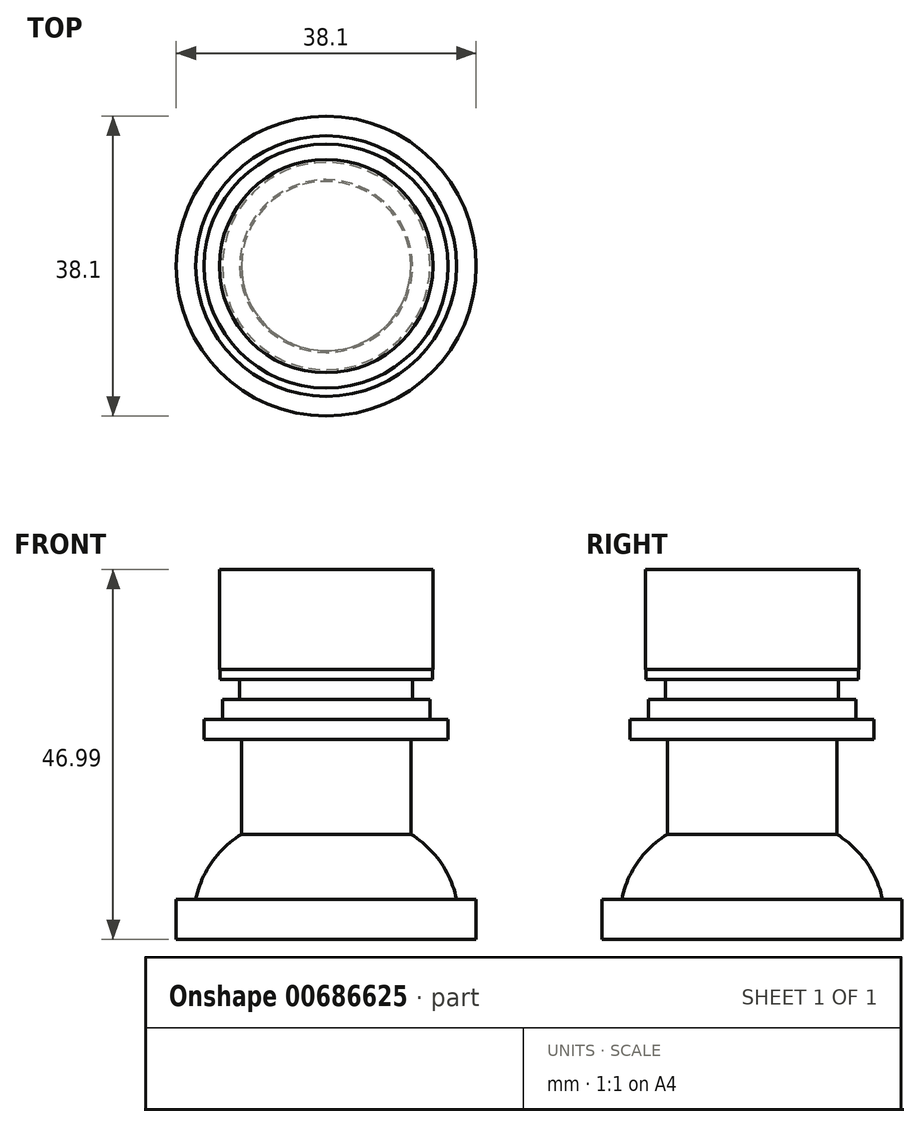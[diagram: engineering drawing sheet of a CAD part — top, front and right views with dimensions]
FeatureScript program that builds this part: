
annotation { "Feature Type Name" : "Feature", "Feature Type Description" : "" }
export const myFeature = defineFeature(function(context is Context, id is Id, definition is map)
    precondition{}
    {
        {
            var Q0;
            Q0=qCreatedBy(makeId("Top.planeOp"),FACE);
            var sketch = newSketch(context, id + "F0", { "sketchPlane" : qUnion([Q0])});
            skCircle(sketch, "E0", {"center": v(0, 0) * mm, "radius": 19.05 * mm});
            skSolve(sketch);
        }
        {
            var Q0;
            Q0=qCreatedBy(makeId("Top.planeOp"),FACE);
            var sketch = newSketch(context, id + "F1", { "sketchPlane" : qUnion([Q0])});
            skCircle(sketch, "E1", {"center": v(0, 0) * mm, "radius": 16.56 * mm});
            skSolve(sketch);
        }
        {
            var Q0;
            Q0 = qSketchRegion(id + "F0", true);
            extrude(context, id + "F2", {"entities" : qUnion([Q0]), "depth" : 5.08 * mm, "offsetDistance" : 25.4 * mm});
        }
        {
            var Q0;
            Q0 = qSketchRegion(id + "F1", true);
            extrude(context, id + "F3", {"entities" : qUnion([Q0]), "operationType" : NewBodyOperationType.ADD, "depth" : 15.24 * mm, "offsetDistance" : 25.4 * mm});
        }
        {
            var Q0;
            Q0=makeQuery(id+"F3.opExtrude","CAP_EDGE",EDGE,{"disambiguationData":[OSD([sQuery(id+"F1.wireOp",EDGE,"E1")])],"isStart":false});
            fillet(context, id + "F4", {"entities" : qUnion([Q0]), "radius" : 12.7 * mm, "tangentPropagation" : true, "allowEdgeOverflow" : false});
        }
        {
            var Q0;
            Q0=qCreatedBy(makeId("Top.planeOp"),FACE);
            var sketch = newSketch(context, id + "F5", { "sketchPlane" : qUnion([Q0])});
            skCircle(sketch, "E2", {"center": v(0, 0) * mm, "radius": 10.76 * mm});
            skSolve(sketch);
        }
        {
            var Q0;
            Q0 = qSketchRegion(id + "F5", true);
            extrude(context, id + "F6", {"entities" : qUnion([Q0]), "operationType" : NewBodyOperationType.ADD, "depth" : 25.4 * mm, "offsetDistance" : 25.4 * mm});
        }
        {
            var Q0;
            Q0=makeQuery(id+"F6.opExtrude","CAP_FACE",FACE,{"disambiguationData":[OSD([sQuery(id+"F5.wireOp",EDGE,"E2")])],"isStart":false});
            var sketch = newSketch(context, id + "F7", { "sketchPlane" : qUnion([Q0])});
            skCircle(sketch, "E3", {"center": v(0, 0) * mm, "radius": 15.5 * mm});
            skSolve(sketch);
        }
        {
            var Q0;
            Q0 = qSketchRegion(id + "F7", true);
            extrude(context, id + "F8", {"entities" : qUnion([Q0]), "operationType" : NewBodyOperationType.ADD, "depth" : 2.54 * mm, "offsetDistance" : 25.4 * mm});
        }
        {
            var Q0;
            Q0=makeQuery(id+"F8.opExtrude","CAP_FACE",FACE,{"disambiguationData":[OSD([sQuery(id+"F7.wireOp",EDGE,"E3")])],"isStart":false});
            var sketch = newSketch(context, id + "F9", { "sketchPlane" : qUnion([Q0])});
            skCircle(sketch, "E4", {"center": v(0, 0) * mm, "radius": 13.17 * mm});
            skSolve(sketch);
        }
        {
            var Q0;
            Q0 = qSketchRegion(id + "F9", true);
            extrude(context, id + "F10", {"entities" : qUnion([Q0]), "operationType" : NewBodyOperationType.ADD, "depth" : 2.54 * mm, "offsetDistance" : 25.4 * mm});
        }
        {
            var Q0;
            Q0=makeQuery(id+"F10.opExtrude","CAP_FACE",FACE,{"disambiguationData":[OSD([sQuery(id+"F9.wireOp",EDGE,"E4")])],"isStart":false});
            var sketch = newSketch(context, id + "F11", { "sketchPlane" : qUnion([Q0])});
            skCircle(sketch, "E5", {"center": v(0, 0) * mm, "radius": 10.98 * mm});
            skSolve(sketch);
        }
        {
            var Q0;
            Q0=makeQuery(id+"F11.imprint","IMPRINT",FACE,{"disambiguationData":[TD([[makeQuery(id+"F11.imprint","IMPRINT",EDGE,{"derivedFrom":sQuery(id+"F11.wireOp",EDGE,"E5")}),1.0]])]});
            extrude(context, id + "F12", {"entities" : qUnion([Q0]), "operationType" : NewBodyOperationType.ADD, "depth" : 2.54 * mm, "offsetDistance" : 25.4 * mm});
        }
        {
            var Q0;
            Q0=makeQuery(id+"F12.opExtrude","CAP_FACE",FACE,{"disambiguationData":[OSD([sQuery(id+"F11.wireOp",EDGE,"E5")])],"isStart":false});
            var sketch = newSketch(context, id + "F13", { "sketchPlane" : qUnion([Q0])});
            skCircle(sketch, "E6", {"center": v(0, 0) * mm, "radius": 13.5 * mm});
            skSolve(sketch);
        }
        {
            var Q0;
            Q0 = qSketchRegion(id + "F13", true);
            extrude(context, id + "F14", {"entities" : qUnion([Q0]), "operationType" : NewBodyOperationType.ADD, "depth" : 1.27 * mm, "offsetDistance" : 25.4 * mm});
        }
        {
            var Q0;
            Q0=makeQuery(id+"F14.opExtrude","CAP_FACE",FACE,{"disambiguationData":[OSD([sQuery(id+"F13.wireOp",EDGE,"E6")])],"isStart":false});
            var sketch = newSketch(context, id + "F15", { "sketchPlane" : qUnion([Q0])});
            skCircle(sketch, "E7", {"center": v(0, 0) * mm, "radius": 13.56 * mm});
            skSolve(sketch);
        }
        {
            var Q0;
            Q0 = qSketchRegion(id + "F15", true);
            extrude(context, id + "F16", {"entities" : qUnion([Q0]), "operationType" : NewBodyOperationType.ADD, "depth" : 12.7 * mm, "offsetDistance" : 25.4 * mm});
        }
    });
